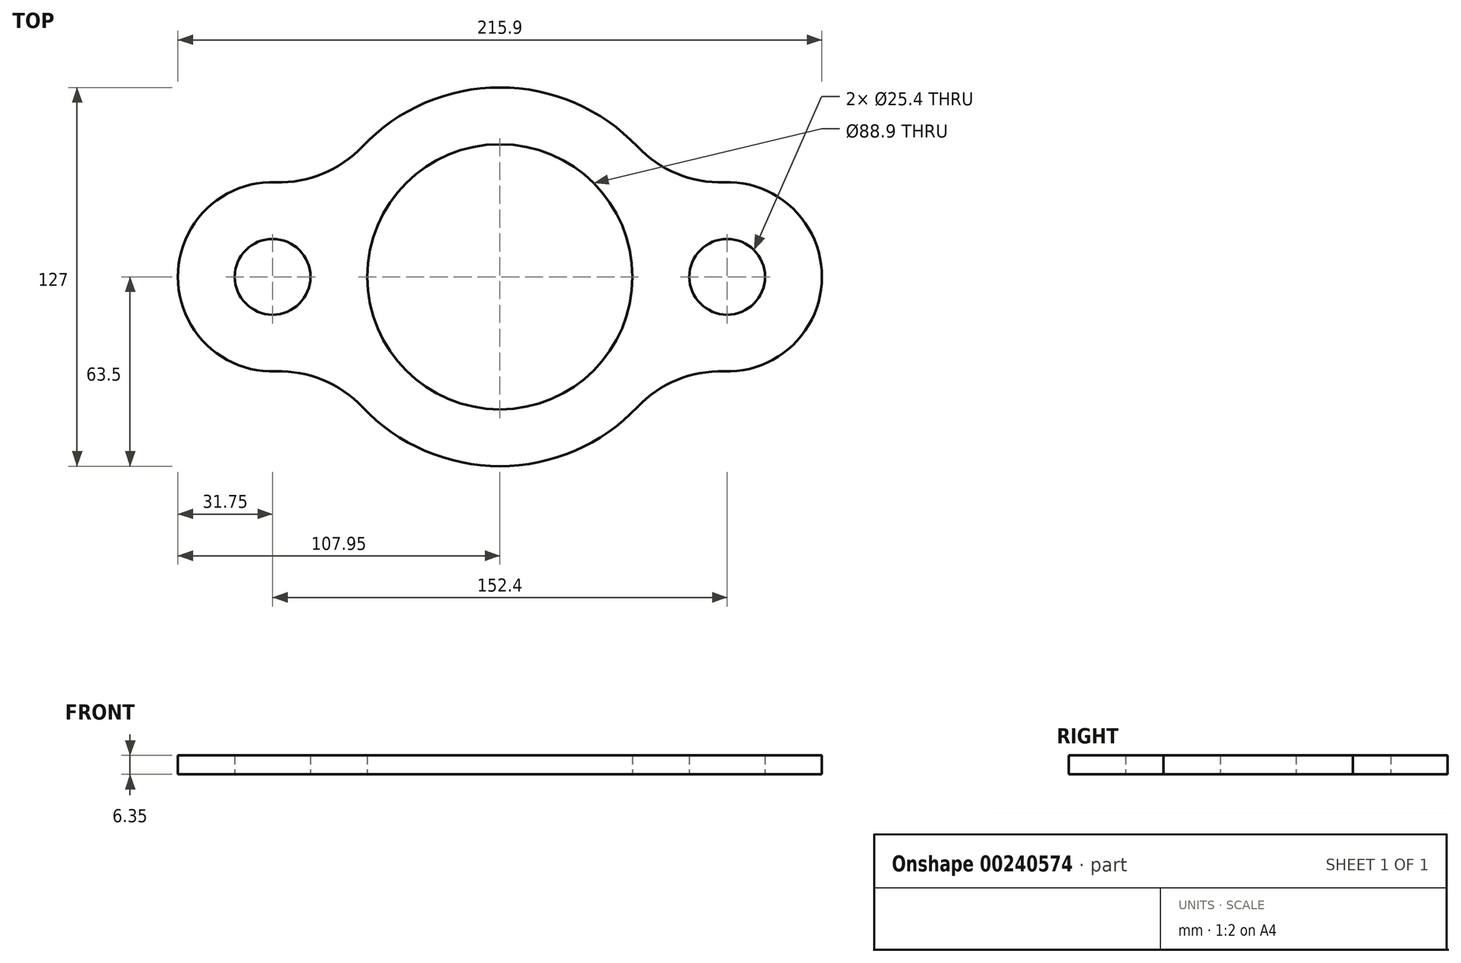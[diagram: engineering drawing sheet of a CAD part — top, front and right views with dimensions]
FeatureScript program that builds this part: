
annotation { "Feature Type Name" : "Feature", "Feature Type Description" : "" }
export const myFeature = defineFeature(function(context is Context, id is Id, definition is map)
    precondition{}
    {
        {
            var Q0;
            Q0=qCreatedBy(makeId("Top.planeOp"),FACE);
            var sketch = newSketch(context, id + "F0", { "sketchPlane" : qUnion([Q0])});
            skCircle(sketch, "E0", {"center": v(0, 0) * mm, "radius": 44.45 * mm});
            skLineSegment(sketch, "E1", {"start": v(0, 0) * mm, "end": v(-76.2, 0) * mm});
            skCircle(sketch, "E2", {"center": v(-76.2, 0) * mm, "radius": 12.7 * mm});
            skCircle(sketch, "E3", {"center": v(76.2, 0) * mm, "radius": 12.7 * mm});
            skArc(sketch, "E4.0", {"start": v(46.14, 43.63) * mm, "mid": v(0, 63.5) * mm, "end": v(-46.14, 43.63) * mm});
            skArc(sketch, "E5.0", {"start": v(75.12, -31.73) * mm, "mid": v(107.95, 0) * mm, "end": v(75.12, 31.73) * mm});
            skPoint(sketch, "E6.visualSharp", {"position": v(57.94, 25.98) * mm});
            skArc(sketch, "E6.filletArc", {"start": v(46.14, 43.63) * mm, "mid": v(59.35, 34.56) * mm, "end": v(75.12, 31.73) * mm});
            skPoint(sketch, "E7.visualSharp", {"position": v(57.94, -25.98) * mm});
            skArc(sketch, "E7.filletArc", {"start": v(75.12, -31.73) * mm, "mid": v(59.35, -34.56) * mm, "end": v(46.14, -43.63) * mm});
            skArc(sketch, "E8.0", {"start": v(-75.12, 31.73) * mm, "mid": v(-107.95, 0) * mm, "end": v(-75.12, -31.73) * mm});
            skArc(sketch, "E9.trimOffspring", {"start": v(-46.14, -43.63) * mm, "mid": v(0, -63.5) * mm, "end": v(46.14, -43.63) * mm});
            skPoint(sketch, "E10.visualSharp", {"position": v(-57.94, 25.98) * mm});
            skArc(sketch, "E10.filletArc", {"start": v(-75.12, 31.73) * mm, "mid": v(-59.35, 34.56) * mm, "end": v(-46.14, 43.63) * mm});
            skPoint(sketch, "E11.visualSharp", {"position": v(-57.94, -25.98) * mm});
            skArc(sketch, "E11.filletArc", {"start": v(-46.14, -43.63) * mm, "mid": v(-59.35, -34.56) * mm, "end": v(-75.12, -31.73) * mm});
            skSolve(sketch);
        }
        {
            var Q0;
            Q0 = qSketchRegion(id + "F0", true);
            extrude(context, id + "F1", {"entities" : qUnion([Q0]), "depth" : 6.35 * mm});
        }
    });
